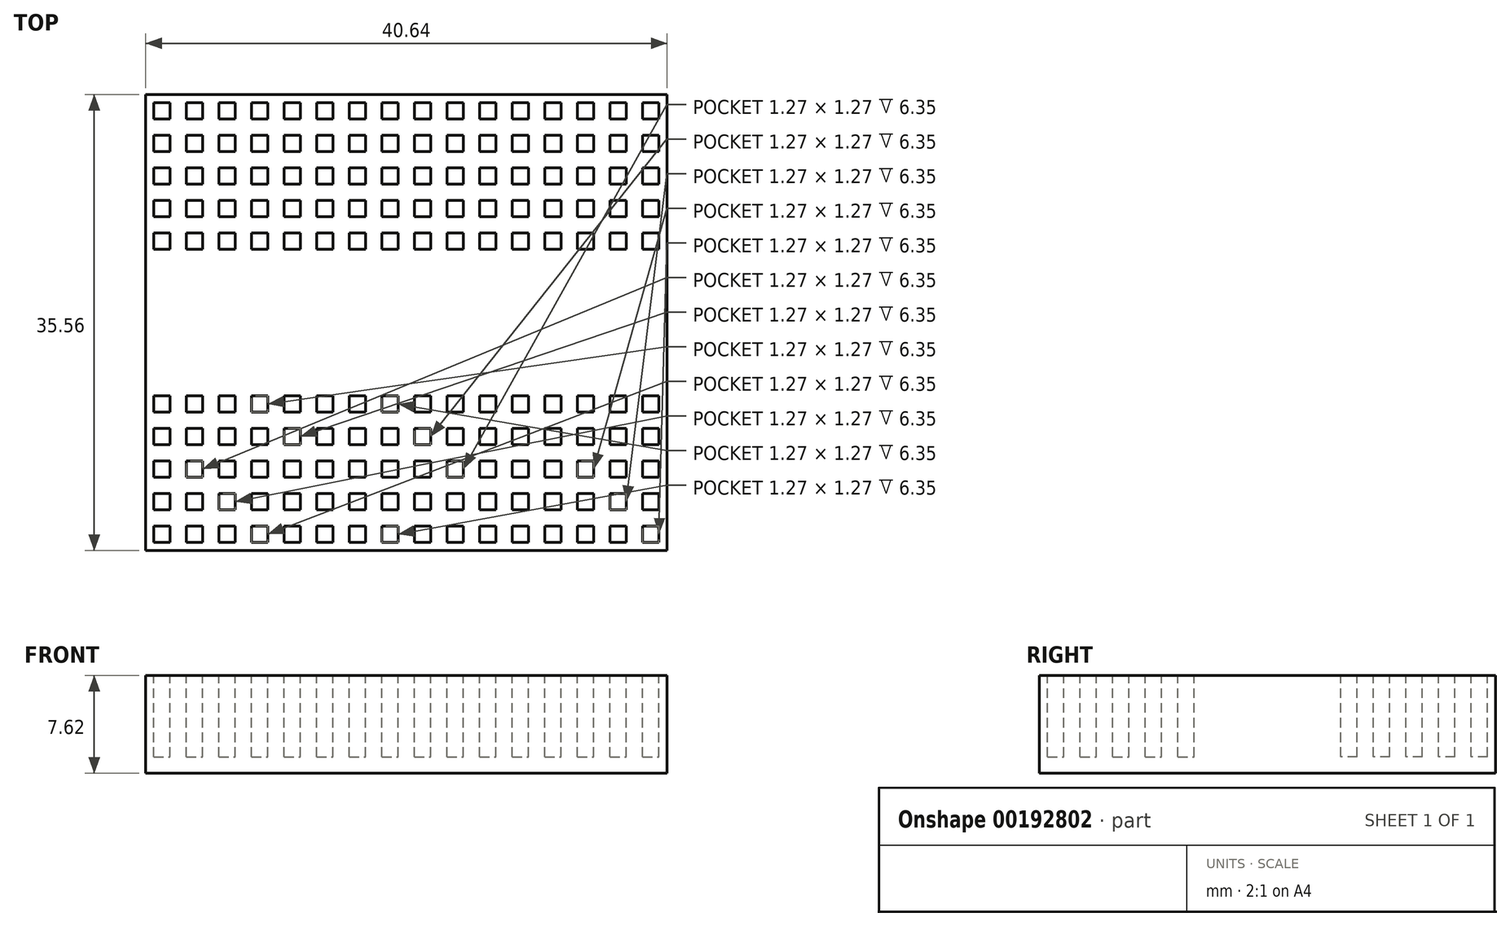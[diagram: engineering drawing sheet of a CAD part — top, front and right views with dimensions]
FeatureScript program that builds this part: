
annotation { "Feature Type Name" : "Feature", "Feature Type Description" : "" }
export const myFeature = defineFeature(function(context is Context, id is Id, definition is map)
    precondition{}
    {
        {
            var Q0;
            Q0=qCreatedBy(makeId("Top.planeOp"),FACE);
            var sketch = newSketch(context, id + "F0", { "sketchPlane" : qUnion([Q0])});
            skLineSegment(sketch, "E0.bottom", {"start": v(-20.32, 17.78) * mm, "end": v(20.32, 17.78) * mm});
            skLineSegment(sketch, "E0.top", {"start": v(-20.32, -17.78) * mm, "end": v(20.32, -17.78) * mm});
            skLineSegment(sketch, "E0.left", {"start": v(-20.32, 17.78) * mm, "end": v(-20.32, -17.78) * mm});
            skLineSegment(sketch, "E0.right", {"start": v(20.32, 17.78) * mm, "end": v(20.32, -17.78) * mm});
            skLineSegment(sketch, "E1", {"start": v(-20.32, 17.78) * mm, "end": v(20.32, -17.78) * mm, "construction": true});
            skSolve(sketch);
        }
        {
            var Q0;
            Q0=qSketchRegion(id+"F0",true);
            extrude(context, id + "F1", {"entities" : qUnion([Q0]), "depth" : 7.62 * mm});
        }
        {
            var Q0;
            Q0=makeQuery(id+"F1.opExtrude","CAP_FACE",FACE,{"disambiguationData":[OSD([sQuery(id+"F0.wireOp",EDGE,"E0.bottom"),sQuery(id+"F0.wireOp",EDGE,"E0.top"),sQuery(id+"F0.wireOp",EDGE,"E0.left"),sQuery(id+"F0.wireOp",EDGE,"E0.right")])],"isStart":false});
            var sketch = newSketch(context, id + "F2", { "sketchPlane" : qUnion([Q0])});
            skLineSegment(sketch, "E2.bottom", {"start": v(-19.69, 17.15) * mm, "end": v(-18.42, 17.15) * mm});
            skLineSegment(sketch, "E2.top", {"start": v(-19.69, 15.88) * mm, "end": v(-18.42, 15.88) * mm});
            skLineSegment(sketch, "E2.left", {"start": v(-19.69, 17.15) * mm, "end": v(-19.69, 15.88) * mm});
            skLineSegment(sketch, "E2.right", {"start": v(-18.42, 17.15) * mm, "end": v(-18.42, 15.88) * mm});
            skLineSegment(sketch, "E3.0.1.0", {"start": v(-19.69, 14.6) * mm, "end": v(-18.42, 14.6) * mm});
            skLineSegment(sketch, "E3.0.1.1", {"start": v(-19.69, 14.6) * mm, "end": v(-19.69, 13.34) * mm});
            skLineSegment(sketch, "E3.0.1.2", {"start": v(-18.42, 14.6) * mm, "end": v(-18.42, 13.34) * mm});
            skLineSegment(sketch, "E3.0.1.3", {"start": v(-19.69, 13.34) * mm, "end": v(-18.42, 13.34) * mm});
            skLineSegment(sketch, "E3.0.2.0", {"start": v(-19.69, 12.07) * mm, "end": v(-18.42, 12.07) * mm});
            skLineSegment(sketch, "E3.0.2.1", {"start": v(-19.69, 12.07) * mm, "end": v(-19.69, 10.8) * mm});
            skLineSegment(sketch, "E3.0.2.2", {"start": v(-18.42, 12.07) * mm, "end": v(-18.42, 10.8) * mm});
            skLineSegment(sketch, "E3.0.2.3", {"start": v(-19.69, 10.8) * mm, "end": v(-18.42, 10.8) * mm});
            skLineSegment(sketch, "E3.0.3.0", {"start": v(-19.69, 9.53) * mm, "end": v(-18.42, 9.53) * mm});
            skLineSegment(sketch, "E3.0.3.1", {"start": v(-19.69, 9.53) * mm, "end": v(-19.69, 8.26) * mm});
            skLineSegment(sketch, "E3.0.3.2", {"start": v(-18.42, 9.53) * mm, "end": v(-18.42, 8.26) * mm});
            skLineSegment(sketch, "E3.0.3.3", {"start": v(-19.69, 8.26) * mm, "end": v(-18.42, 8.26) * mm});
            skLineSegment(sketch, "E3.0.4.0", {"start": v(-19.69, 6.99) * mm, "end": v(-18.42, 6.99) * mm});
            skLineSegment(sketch, "E3.0.4.1", {"start": v(-19.69, 6.99) * mm, "end": v(-19.69, 5.72) * mm});
            skLineSegment(sketch, "E3.0.4.2", {"start": v(-18.42, 6.99) * mm, "end": v(-18.42, 5.72) * mm});
            skLineSegment(sketch, "E3.0.4.3", {"start": v(-19.69, 5.72) * mm, "end": v(-18.42, 5.72) * mm});
            skLineSegment(sketch, "E3.1.0.0", {"start": v(-17.15, 17.15) * mm, "end": v(-15.88, 17.15) * mm});
            skLineSegment(sketch, "E3.1.0.1", {"start": v(-17.15, 17.15) * mm, "end": v(-17.15, 15.88) * mm});
            skLineSegment(sketch, "E3.1.0.2", {"start": v(-15.88, 17.15) * mm, "end": v(-15.88, 15.88) * mm});
            skLineSegment(sketch, "E3.1.0.3", {"start": v(-17.15, 15.88) * mm, "end": v(-15.88, 15.88) * mm});
            skLineSegment(sketch, "E3.1.1.0", {"start": v(-17.15, 14.6) * mm, "end": v(-15.88, 14.6) * mm});
            skLineSegment(sketch, "E3.1.1.1", {"start": v(-17.15, 14.6) * mm, "end": v(-17.15, 13.34) * mm});
            skLineSegment(sketch, "E3.1.1.2", {"start": v(-15.88, 14.6) * mm, "end": v(-15.88, 13.34) * mm});
            skLineSegment(sketch, "E3.1.1.3", {"start": v(-17.15, 13.34) * mm, "end": v(-15.88, 13.34) * mm});
            skLineSegment(sketch, "E3.1.2.0", {"start": v(-17.15, 12.07) * mm, "end": v(-15.88, 12.07) * mm});
            skLineSegment(sketch, "E3.1.2.1", {"start": v(-17.15, 12.07) * mm, "end": v(-17.15, 10.8) * mm});
            skLineSegment(sketch, "E3.1.2.2", {"start": v(-15.88, 12.07) * mm, "end": v(-15.88, 10.8) * mm});
            skLineSegment(sketch, "E3.1.2.3", {"start": v(-17.15, 10.8) * mm, "end": v(-15.88, 10.8) * mm});
            skLineSegment(sketch, "E3.1.3.0", {"start": v(-17.15, 9.53) * mm, "end": v(-15.88, 9.53) * mm});
            skLineSegment(sketch, "E3.1.3.1", {"start": v(-17.15, 9.53) * mm, "end": v(-17.15, 8.26) * mm});
            skLineSegment(sketch, "E3.1.3.2", {"start": v(-15.88, 9.53) * mm, "end": v(-15.88, 8.26) * mm});
            skLineSegment(sketch, "E3.1.3.3", {"start": v(-17.15, 8.26) * mm, "end": v(-15.88, 8.26) * mm});
            skLineSegment(sketch, "E3.1.4.0", {"start": v(-17.15, 6.99) * mm, "end": v(-15.88, 6.99) * mm});
            skLineSegment(sketch, "E3.1.4.1", {"start": v(-17.15, 6.99) * mm, "end": v(-17.15, 5.72) * mm});
            skLineSegment(sketch, "E3.1.4.2", {"start": v(-15.88, 6.99) * mm, "end": v(-15.88, 5.72) * mm});
            skLineSegment(sketch, "E3.1.4.3", {"start": v(-17.15, 5.72) * mm, "end": v(-15.88, 5.72) * mm});
            skLineSegment(sketch, "E3.2.0.0", {"start": v(-14.6, 17.15) * mm, "end": v(-13.34, 17.15) * mm});
            skLineSegment(sketch, "E3.2.0.1", {"start": v(-14.6, 17.15) * mm, "end": v(-14.6, 15.88) * mm});
            skLineSegment(sketch, "E3.2.0.2", {"start": v(-13.34, 17.15) * mm, "end": v(-13.34, 15.88) * mm});
            skLineSegment(sketch, "E3.2.0.3", {"start": v(-14.6, 15.88) * mm, "end": v(-13.34, 15.88) * mm});
            skLineSegment(sketch, "E3.2.1.0", {"start": v(-14.6, 14.6) * mm, "end": v(-13.34, 14.6) * mm});
            skLineSegment(sketch, "E3.2.1.1", {"start": v(-14.6, 14.6) * mm, "end": v(-14.6, 13.34) * mm});
            skLineSegment(sketch, "E3.2.1.2", {"start": v(-13.34, 14.6) * mm, "end": v(-13.34, 13.34) * mm});
            skLineSegment(sketch, "E3.2.1.3", {"start": v(-14.6, 13.34) * mm, "end": v(-13.34, 13.34) * mm});
            skLineSegment(sketch, "E3.2.2.0", {"start": v(-14.6, 12.07) * mm, "end": v(-13.34, 12.07) * mm});
            skLineSegment(sketch, "E3.2.2.1", {"start": v(-14.6, 12.07) * mm, "end": v(-14.6, 10.8) * mm});
            skLineSegment(sketch, "E3.2.2.2", {"start": v(-13.34, 12.07) * mm, "end": v(-13.34, 10.8) * mm});
            skLineSegment(sketch, "E3.2.2.3", {"start": v(-14.6, 10.8) * mm, "end": v(-13.34, 10.8) * mm});
            skLineSegment(sketch, "E3.2.3.0", {"start": v(-14.6, 9.53) * mm, "end": v(-13.34, 9.53) * mm});
            skLineSegment(sketch, "E3.2.3.1", {"start": v(-14.6, 9.53) * mm, "end": v(-14.6, 8.26) * mm});
            skLineSegment(sketch, "E3.2.3.2", {"start": v(-13.34, 9.53) * mm, "end": v(-13.34, 8.26) * mm});
            skLineSegment(sketch, "E3.2.3.3", {"start": v(-14.6, 8.26) * mm, "end": v(-13.34, 8.26) * mm});
            skLineSegment(sketch, "E3.2.4.0", {"start": v(-14.6, 6.99) * mm, "end": v(-13.34, 6.99) * mm});
            skLineSegment(sketch, "E3.2.4.1", {"start": v(-14.6, 6.99) * mm, "end": v(-14.6, 5.72) * mm});
            skLineSegment(sketch, "E3.2.4.2", {"start": v(-13.34, 6.99) * mm, "end": v(-13.34, 5.72) * mm});
            skLineSegment(sketch, "E3.2.4.3", {"start": v(-14.6, 5.72) * mm, "end": v(-13.34, 5.72) * mm});
            skLineSegment(sketch, "E3.3.0.0", {"start": v(-12.07, 17.15) * mm, "end": v(-10.8, 17.15) * mm});
            skLineSegment(sketch, "E3.3.0.1", {"start": v(-12.07, 17.15) * mm, "end": v(-12.07, 15.88) * mm});
            skLineSegment(sketch, "E3.3.0.2", {"start": v(-10.8, 17.15) * mm, "end": v(-10.8, 15.88) * mm});
            skLineSegment(sketch, "E3.3.0.3", {"start": v(-12.07, 15.88) * mm, "end": v(-10.8, 15.88) * mm});
            skLineSegment(sketch, "E3.3.1.0", {"start": v(-12.07, 14.6) * mm, "end": v(-10.8, 14.6) * mm});
            skLineSegment(sketch, "E3.3.1.1", {"start": v(-12.07, 14.6) * mm, "end": v(-12.07, 13.34) * mm});
            skLineSegment(sketch, "E3.3.1.2", {"start": v(-10.8, 14.6) * mm, "end": v(-10.8, 13.34) * mm});
            skLineSegment(sketch, "E3.3.1.3", {"start": v(-12.07, 13.34) * mm, "end": v(-10.8, 13.34) * mm});
            skLineSegment(sketch, "E3.3.2.0", {"start": v(-12.07, 12.07) * mm, "end": v(-10.8, 12.07) * mm});
            skLineSegment(sketch, "E3.3.2.1", {"start": v(-12.07, 12.07) * mm, "end": v(-12.07, 10.8) * mm});
            skLineSegment(sketch, "E3.3.2.2", {"start": v(-10.8, 12.07) * mm, "end": v(-10.8, 10.8) * mm});
            skLineSegment(sketch, "E3.3.2.3", {"start": v(-12.07, 10.8) * mm, "end": v(-10.8, 10.8) * mm});
            skLineSegment(sketch, "E3.3.3.0", {"start": v(-12.07, 9.53) * mm, "end": v(-10.8, 9.53) * mm});
            skLineSegment(sketch, "E3.3.3.1", {"start": v(-12.07, 9.53) * mm, "end": v(-12.07, 8.26) * mm});
            skLineSegment(sketch, "E3.3.3.2", {"start": v(-10.8, 9.53) * mm, "end": v(-10.8, 8.26) * mm});
            skLineSegment(sketch, "E3.3.3.3", {"start": v(-12.07, 8.26) * mm, "end": v(-10.8, 8.26) * mm});
            skLineSegment(sketch, "E3.3.4.0", {"start": v(-12.07, 6.99) * mm, "end": v(-10.8, 6.99) * mm});
            skLineSegment(sketch, "E3.3.4.1", {"start": v(-12.07, 6.99) * mm, "end": v(-12.07, 5.72) * mm});
            skLineSegment(sketch, "E3.3.4.2", {"start": v(-10.8, 6.99) * mm, "end": v(-10.8, 5.72) * mm});
            skLineSegment(sketch, "E3.3.4.3", {"start": v(-12.07, 5.72) * mm, "end": v(-10.8, 5.72) * mm});
            skLineSegment(sketch, "E3.4.0.0", {"start": v(-9.53, 17.15) * mm, "end": v(-8.26, 17.15) * mm});
            skLineSegment(sketch, "E3.4.0.1", {"start": v(-9.53, 17.15) * mm, "end": v(-9.53, 15.88) * mm});
            skLineSegment(sketch, "E3.4.0.2", {"start": v(-8.26, 17.15) * mm, "end": v(-8.26, 15.88) * mm});
            skLineSegment(sketch, "E3.4.0.3", {"start": v(-9.53, 15.88) * mm, "end": v(-8.26, 15.88) * mm});
            skLineSegment(sketch, "E3.4.1.0", {"start": v(-9.53, 14.6) * mm, "end": v(-8.26, 14.6) * mm});
            skLineSegment(sketch, "E3.4.1.1", {"start": v(-9.53, 14.6) * mm, "end": v(-9.53, 13.34) * mm});
            skLineSegment(sketch, "E3.4.1.2", {"start": v(-8.26, 14.6) * mm, "end": v(-8.26, 13.34) * mm});
            skLineSegment(sketch, "E3.4.1.3", {"start": v(-9.53, 13.34) * mm, "end": v(-8.26, 13.34) * mm});
            skLineSegment(sketch, "E3.4.2.0", {"start": v(-9.53, 12.07) * mm, "end": v(-8.26, 12.07) * mm});
            skLineSegment(sketch, "E3.4.2.1", {"start": v(-9.53, 12.07) * mm, "end": v(-9.53, 10.8) * mm});
            skLineSegment(sketch, "E3.4.2.2", {"start": v(-8.26, 12.07) * mm, "end": v(-8.26, 10.8) * mm});
            skLineSegment(sketch, "E3.4.2.3", {"start": v(-9.53, 10.8) * mm, "end": v(-8.26, 10.8) * mm});
            skLineSegment(sketch, "E3.4.3.0", {"start": v(-9.53, 9.53) * mm, "end": v(-8.26, 9.53) * mm});
            skLineSegment(sketch, "E3.4.3.1", {"start": v(-9.53, 9.53) * mm, "end": v(-9.53, 8.26) * mm});
            skLineSegment(sketch, "E3.4.3.2", {"start": v(-8.26, 9.53) * mm, "end": v(-8.26, 8.26) * mm});
            skLineSegment(sketch, "E3.4.3.3", {"start": v(-9.53, 8.26) * mm, "end": v(-8.26, 8.26) * mm});
            skLineSegment(sketch, "E3.4.4.0", {"start": v(-9.53, 6.99) * mm, "end": v(-8.26, 6.99) * mm});
            skLineSegment(sketch, "E3.4.4.1", {"start": v(-9.53, 6.99) * mm, "end": v(-9.53, 5.72) * mm});
            skLineSegment(sketch, "E3.4.4.2", {"start": v(-8.26, 6.99) * mm, "end": v(-8.26, 5.72) * mm});
            skLineSegment(sketch, "E3.4.4.3", {"start": v(-9.53, 5.72) * mm, "end": v(-8.26, 5.72) * mm});
            skLineSegment(sketch, "E3.5.0.0", {"start": v(-6.99, 17.15) * mm, "end": v(-5.72, 17.15) * mm});
            skLineSegment(sketch, "E3.5.0.1", {"start": v(-6.99, 17.15) * mm, "end": v(-6.99, 15.88) * mm});
            skLineSegment(sketch, "E3.5.0.2", {"start": v(-5.72, 17.15) * mm, "end": v(-5.72, 15.88) * mm});
            skLineSegment(sketch, "E3.5.0.3", {"start": v(-6.99, 15.88) * mm, "end": v(-5.72, 15.88) * mm});
            skLineSegment(sketch, "E3.5.1.0", {"start": v(-6.99, 14.6) * mm, "end": v(-5.72, 14.6) * mm});
            skLineSegment(sketch, "E3.5.1.1", {"start": v(-6.99, 14.6) * mm, "end": v(-6.99, 13.34) * mm});
            skLineSegment(sketch, "E3.5.1.2", {"start": v(-5.72, 14.6) * mm, "end": v(-5.72, 13.34) * mm});
            skLineSegment(sketch, "E3.5.1.3", {"start": v(-6.99, 13.34) * mm, "end": v(-5.72, 13.34) * mm});
            skLineSegment(sketch, "E3.5.2.0", {"start": v(-6.99, 12.07) * mm, "end": v(-5.72, 12.07) * mm});
            skLineSegment(sketch, "E3.5.2.1", {"start": v(-6.99, 12.07) * mm, "end": v(-6.99, 10.8) * mm});
            skLineSegment(sketch, "E3.5.2.2", {"start": v(-5.72, 12.07) * mm, "end": v(-5.72, 10.8) * mm});
            skLineSegment(sketch, "E3.5.2.3", {"start": v(-6.99, 10.8) * mm, "end": v(-5.72, 10.8) * mm});
            skLineSegment(sketch, "E3.5.3.0", {"start": v(-6.99, 9.53) * mm, "end": v(-5.72, 9.53) * mm});
            skLineSegment(sketch, "E3.5.3.1", {"start": v(-6.99, 9.53) * mm, "end": v(-6.99, 8.26) * mm});
            skLineSegment(sketch, "E3.5.3.2", {"start": v(-5.72, 9.53) * mm, "end": v(-5.72, 8.26) * mm});
            skLineSegment(sketch, "E3.5.3.3", {"start": v(-6.99, 8.26) * mm, "end": v(-5.72, 8.26) * mm});
            skLineSegment(sketch, "E3.5.4.0", {"start": v(-6.99, 6.99) * mm, "end": v(-5.72, 6.99) * mm});
            skLineSegment(sketch, "E3.5.4.1", {"start": v(-6.99, 6.99) * mm, "end": v(-6.99, 5.72) * mm});
            skLineSegment(sketch, "E3.5.4.2", {"start": v(-5.72, 6.99) * mm, "end": v(-5.72, 5.72) * mm});
            skLineSegment(sketch, "E3.5.4.3", {"start": v(-6.99, 5.72) * mm, "end": v(-5.72, 5.72) * mm});
            skLineSegment(sketch, "E3.6.0.0", {"start": v(-4.45, 17.15) * mm, "end": v(-3.18, 17.15) * mm});
            skLineSegment(sketch, "E3.6.0.1", {"start": v(-4.45, 17.15) * mm, "end": v(-4.45, 15.88) * mm});
            skLineSegment(sketch, "E3.6.0.2", {"start": v(-3.18, 17.15) * mm, "end": v(-3.18, 15.88) * mm});
            skLineSegment(sketch, "E3.6.0.3", {"start": v(-4.45, 15.88) * mm, "end": v(-3.18, 15.88) * mm});
            skLineSegment(sketch, "E3.6.1.0", {"start": v(-4.45, 14.6) * mm, "end": v(-3.18, 14.6) * mm});
            skLineSegment(sketch, "E3.6.1.1", {"start": v(-4.45, 14.6) * mm, "end": v(-4.45, 13.34) * mm});
            skLineSegment(sketch, "E3.6.1.2", {"start": v(-3.18, 14.6) * mm, "end": v(-3.18, 13.34) * mm});
            skLineSegment(sketch, "E3.6.1.3", {"start": v(-4.45, 13.34) * mm, "end": v(-3.18, 13.34) * mm});
            skLineSegment(sketch, "E3.6.2.0", {"start": v(-4.45, 12.07) * mm, "end": v(-3.18, 12.07) * mm});
            skLineSegment(sketch, "E3.6.2.1", {"start": v(-4.45, 12.07) * mm, "end": v(-4.45, 10.8) * mm});
            skLineSegment(sketch, "E3.6.2.2", {"start": v(-3.18, 12.07) * mm, "end": v(-3.18, 10.8) * mm});
            skLineSegment(sketch, "E3.6.2.3", {"start": v(-4.45, 10.8) * mm, "end": v(-3.18, 10.8) * mm});
            skLineSegment(sketch, "E3.6.3.0", {"start": v(-4.45, 9.53) * mm, "end": v(-3.18, 9.53) * mm});
            skLineSegment(sketch, "E3.6.3.1", {"start": v(-4.45, 9.53) * mm, "end": v(-4.45, 8.26) * mm});
            skLineSegment(sketch, "E3.6.3.2", {"start": v(-3.18, 9.53) * mm, "end": v(-3.18, 8.26) * mm});
            skLineSegment(sketch, "E3.6.3.3", {"start": v(-4.45, 8.26) * mm, "end": v(-3.18, 8.26) * mm});
            skLineSegment(sketch, "E3.6.4.0", {"start": v(-4.45, 6.99) * mm, "end": v(-3.18, 6.99) * mm});
            skLineSegment(sketch, "E3.6.4.1", {"start": v(-4.45, 6.99) * mm, "end": v(-4.45, 5.72) * mm});
            skLineSegment(sketch, "E3.6.4.2", {"start": v(-3.18, 6.99) * mm, "end": v(-3.18, 5.72) * mm});
            skLineSegment(sketch, "E3.6.4.3", {"start": v(-4.45, 5.72) * mm, "end": v(-3.18, 5.72) * mm});
            skLineSegment(sketch, "E3.7.0.0", {"start": v(-1.9, 17.15) * mm, "end": v(-0.64, 17.15) * mm});
            skLineSegment(sketch, "E3.7.0.1", {"start": v(-1.9, 17.15) * mm, "end": v(-1.9, 15.88) * mm});
            skLineSegment(sketch, "E3.7.0.2", {"start": v(-0.63, 17.15) * mm, "end": v(-0.64, 15.88) * mm});
            skLineSegment(sketch, "E3.7.0.3", {"start": v(-1.9, 15.88) * mm, "end": v(-0.64, 15.88) * mm});
            skLineSegment(sketch, "E3.7.1.0", {"start": v(-1.9, 14.6) * mm, "end": v(-0.64, 14.6) * mm});
            skLineSegment(sketch, "E3.7.1.1", {"start": v(-1.9, 14.6) * mm, "end": v(-1.9, 13.34) * mm});
            skLineSegment(sketch, "E3.7.1.2", {"start": v(-0.63, 14.6) * mm, "end": v(-0.64, 13.34) * mm});
            skLineSegment(sketch, "E3.7.1.3", {"start": v(-1.9, 13.34) * mm, "end": v(-0.64, 13.34) * mm});
            skLineSegment(sketch, "E3.7.2.0", {"start": v(-1.9, 12.07) * mm, "end": v(-0.64, 12.07) * mm});
            skLineSegment(sketch, "E3.7.2.1", {"start": v(-1.9, 12.07) * mm, "end": v(-1.9, 10.8) * mm});
            skLineSegment(sketch, "E3.7.2.2", {"start": v(-0.63, 12.07) * mm, "end": v(-0.64, 10.8) * mm});
            skLineSegment(sketch, "E3.7.2.3", {"start": v(-1.9, 10.8) * mm, "end": v(-0.64, 10.8) * mm});
            skLineSegment(sketch, "E3.7.3.0", {"start": v(-1.9, 9.53) * mm, "end": v(-0.64, 9.53) * mm});
            skLineSegment(sketch, "E3.7.3.1", {"start": v(-1.9, 9.53) * mm, "end": v(-1.9, 8.26) * mm});
            skLineSegment(sketch, "E3.7.3.2", {"start": v(-0.63, 9.53) * mm, "end": v(-0.64, 8.26) * mm});
            skLineSegment(sketch, "E3.7.3.3", {"start": v(-1.9, 8.26) * mm, "end": v(-0.64, 8.26) * mm});
            skLineSegment(sketch, "E3.7.4.0", {"start": v(-1.9, 6.99) * mm, "end": v(-0.64, 6.99) * mm});
            skLineSegment(sketch, "E3.7.4.1", {"start": v(-1.9, 6.99) * mm, "end": v(-1.9, 5.72) * mm});
            skLineSegment(sketch, "E3.7.4.2", {"start": v(-0.63, 6.99) * mm, "end": v(-0.64, 5.72) * mm});
            skLineSegment(sketch, "E3.7.4.3", {"start": v(-1.9, 5.72) * mm, "end": v(-0.64, 5.72) * mm});
            skLineSegment(sketch, "E3.8.0.0", {"start": v(0.64, 17.15) * mm, "end": v(1.9, 17.15) * mm});
            skLineSegment(sketch, "E3.8.0.1", {"start": v(0.64, 17.15) * mm, "end": v(0.64, 15.88) * mm});
            skLineSegment(sketch, "E3.8.0.2", {"start": v(1.9, 17.15) * mm, "end": v(1.9, 15.88) * mm});
            skLineSegment(sketch, "E3.8.0.3", {"start": v(0.64, 15.88) * mm, "end": v(1.9, 15.88) * mm});
            skLineSegment(sketch, "E3.8.1.0", {"start": v(0.64, 14.6) * mm, "end": v(1.9, 14.6) * mm});
            skLineSegment(sketch, "E3.8.1.1", {"start": v(0.64, 14.6) * mm, "end": v(0.64, 13.34) * mm});
            skLineSegment(sketch, "E3.8.1.2", {"start": v(1.9, 14.6) * mm, "end": v(1.9, 13.34) * mm});
            skLineSegment(sketch, "E3.8.1.3", {"start": v(0.64, 13.34) * mm, "end": v(1.9, 13.34) * mm});
            skLineSegment(sketch, "E3.8.2.0", {"start": v(0.64, 12.07) * mm, "end": v(1.9, 12.07) * mm});
            skLineSegment(sketch, "E3.8.2.1", {"start": v(0.64, 12.07) * mm, "end": v(0.64, 10.8) * mm});
            skLineSegment(sketch, "E3.8.2.2", {"start": v(1.9, 12.07) * mm, "end": v(1.9, 10.8) * mm});
            skLineSegment(sketch, "E3.8.2.3", {"start": v(0.64, 10.8) * mm, "end": v(1.9, 10.8) * mm});
            skLineSegment(sketch, "E3.8.3.0", {"start": v(0.64, 9.53) * mm, "end": v(1.9, 9.53) * mm});
            skLineSegment(sketch, "E3.8.3.1", {"start": v(0.64, 9.53) * mm, "end": v(0.64, 8.26) * mm});
            skLineSegment(sketch, "E3.8.3.2", {"start": v(1.9, 9.53) * mm, "end": v(1.9, 8.26) * mm});
            skLineSegment(sketch, "E3.8.3.3", {"start": v(0.64, 8.26) * mm, "end": v(1.9, 8.26) * mm});
            skLineSegment(sketch, "E3.8.4.0", {"start": v(0.64, 6.99) * mm, "end": v(1.9, 6.99) * mm});
            skLineSegment(sketch, "E3.8.4.1", {"start": v(0.64, 6.99) * mm, "end": v(0.64, 5.72) * mm});
            skLineSegment(sketch, "E3.8.4.2", {"start": v(1.9, 6.99) * mm, "end": v(1.9, 5.72) * mm});
            skLineSegment(sketch, "E3.8.4.3", {"start": v(0.64, 5.72) * mm, "end": v(1.9, 5.72) * mm});
            skLineSegment(sketch, "E3.9.0.0", {"start": v(3.18, 17.15) * mm, "end": v(4.45, 17.15) * mm});
            skLineSegment(sketch, "E3.9.0.1", {"start": v(3.18, 17.15) * mm, "end": v(3.18, 15.88) * mm});
            skLineSegment(sketch, "E3.9.0.2", {"start": v(4.45, 17.15) * mm, "end": v(4.45, 15.88) * mm});
            skLineSegment(sketch, "E3.9.0.3", {"start": v(3.18, 15.88) * mm, "end": v(4.45, 15.88) * mm});
            skLineSegment(sketch, "E3.9.1.0", {"start": v(3.18, 14.6) * mm, "end": v(4.45, 14.6) * mm});
            skLineSegment(sketch, "E3.9.1.1", {"start": v(3.18, 14.6) * mm, "end": v(3.18, 13.34) * mm});
            skLineSegment(sketch, "E3.9.1.2", {"start": v(4.45, 14.6) * mm, "end": v(4.45, 13.34) * mm});
            skLineSegment(sketch, "E3.9.1.3", {"start": v(3.18, 13.34) * mm, "end": v(4.45, 13.34) * mm});
            skLineSegment(sketch, "E3.9.2.0", {"start": v(3.18, 12.07) * mm, "end": v(4.45, 12.07) * mm});
            skLineSegment(sketch, "E3.9.2.1", {"start": v(3.18, 12.07) * mm, "end": v(3.18, 10.8) * mm});
            skLineSegment(sketch, "E3.9.2.2", {"start": v(4.45, 12.07) * mm, "end": v(4.45, 10.8) * mm});
            skLineSegment(sketch, "E3.9.2.3", {"start": v(3.18, 10.8) * mm, "end": v(4.45, 10.8) * mm});
            skLineSegment(sketch, "E3.9.3.0", {"start": v(3.18, 9.53) * mm, "end": v(4.45, 9.53) * mm});
            skLineSegment(sketch, "E3.9.3.1", {"start": v(3.18, 9.53) * mm, "end": v(3.18, 8.26) * mm});
            skLineSegment(sketch, "E3.9.3.2", {"start": v(4.45, 9.53) * mm, "end": v(4.45, 8.26) * mm});
            skLineSegment(sketch, "E3.9.3.3", {"start": v(3.18, 8.26) * mm, "end": v(4.45, 8.26) * mm});
            skLineSegment(sketch, "E3.9.4.0", {"start": v(3.18, 6.99) * mm, "end": v(4.45, 6.99) * mm});
            skLineSegment(sketch, "E3.9.4.1", {"start": v(3.18, 6.99) * mm, "end": v(3.18, 5.72) * mm});
            skLineSegment(sketch, "E3.9.4.2", {"start": v(4.45, 6.99) * mm, "end": v(4.45, 5.72) * mm});
            skLineSegment(sketch, "E3.9.4.3", {"start": v(3.18, 5.72) * mm, "end": v(4.45, 5.72) * mm});
            skLineSegment(sketch, "E3.10.0.0", {"start": v(5.72, 17.15) * mm, "end": v(6.99, 17.15) * mm});
            skLineSegment(sketch, "E3.10.0.1", {"start": v(5.72, 17.15) * mm, "end": v(5.72, 15.88) * mm});
            skLineSegment(sketch, "E3.10.0.2", {"start": v(6.99, 17.15) * mm, "end": v(6.99, 15.88) * mm});
            skLineSegment(sketch, "E3.10.0.3", {"start": v(5.72, 15.88) * mm, "end": v(6.99, 15.88) * mm});
            skLineSegment(sketch, "E3.10.1.0", {"start": v(5.72, 14.6) * mm, "end": v(6.99, 14.6) * mm});
            skLineSegment(sketch, "E3.10.1.1", {"start": v(5.72, 14.6) * mm, "end": v(5.72, 13.34) * mm});
            skLineSegment(sketch, "E3.10.1.2", {"start": v(6.99, 14.6) * mm, "end": v(6.99, 13.34) * mm});
            skLineSegment(sketch, "E3.10.1.3", {"start": v(5.72, 13.34) * mm, "end": v(6.99, 13.34) * mm});
            skLineSegment(sketch, "E3.10.2.0", {"start": v(5.72, 12.07) * mm, "end": v(6.99, 12.07) * mm});
            skLineSegment(sketch, "E3.10.2.1", {"start": v(5.72, 12.07) * mm, "end": v(5.72, 10.8) * mm});
            skLineSegment(sketch, "E3.10.2.2", {"start": v(6.99, 12.07) * mm, "end": v(6.99, 10.8) * mm});
            skLineSegment(sketch, "E3.10.2.3", {"start": v(5.72, 10.8) * mm, "end": v(6.99, 10.8) * mm});
            skLineSegment(sketch, "E3.10.3.0", {"start": v(5.72, 9.53) * mm, "end": v(6.99, 9.53) * mm});
            skLineSegment(sketch, "E3.10.3.1", {"start": v(5.72, 9.53) * mm, "end": v(5.72, 8.26) * mm});
            skLineSegment(sketch, "E3.10.3.2", {"start": v(6.99, 9.53) * mm, "end": v(6.99, 8.26) * mm});
            skLineSegment(sketch, "E3.10.3.3", {"start": v(5.72, 8.26) * mm, "end": v(6.99, 8.26) * mm});
            skLineSegment(sketch, "E3.10.4.0", {"start": v(5.72, 6.99) * mm, "end": v(6.99, 6.99) * mm});
            skLineSegment(sketch, "E3.10.4.1", {"start": v(5.72, 6.99) * mm, "end": v(5.72, 5.72) * mm});
            skLineSegment(sketch, "E3.10.4.2", {"start": v(6.99, 6.99) * mm, "end": v(6.99, 5.72) * mm});
            skLineSegment(sketch, "E3.10.4.3", {"start": v(5.72, 5.72) * mm, "end": v(6.99, 5.72) * mm});
            skLineSegment(sketch, "E3.11.0.0", {"start": v(8.26, 17.15) * mm, "end": v(9.53, 17.15) * mm});
            skLineSegment(sketch, "E3.11.0.1", {"start": v(8.26, 17.15) * mm, "end": v(8.26, 15.88) * mm});
            skLineSegment(sketch, "E3.11.0.2", {"start": v(9.53, 17.15) * mm, "end": v(9.53, 15.88) * mm});
            skLineSegment(sketch, "E3.11.0.3", {"start": v(8.26, 15.88) * mm, "end": v(9.53, 15.88) * mm});
            skLineSegment(sketch, "E3.11.1.0", {"start": v(8.26, 14.6) * mm, "end": v(9.53, 14.6) * mm});
            skLineSegment(sketch, "E3.11.1.1", {"start": v(8.26, 14.6) * mm, "end": v(8.26, 13.34) * mm});
            skLineSegment(sketch, "E3.11.1.2", {"start": v(9.53, 14.6) * mm, "end": v(9.53, 13.34) * mm});
            skLineSegment(sketch, "E3.11.1.3", {"start": v(8.26, 13.34) * mm, "end": v(9.53, 13.34) * mm});
            skLineSegment(sketch, "E3.11.2.0", {"start": v(8.26, 12.07) * mm, "end": v(9.53, 12.07) * mm});
            skLineSegment(sketch, "E3.11.2.1", {"start": v(8.26, 12.07) * mm, "end": v(8.26, 10.8) * mm});
            skLineSegment(sketch, "E3.11.2.2", {"start": v(9.53, 12.07) * mm, "end": v(9.53, 10.8) * mm});
            skLineSegment(sketch, "E3.11.2.3", {"start": v(8.26, 10.8) * mm, "end": v(9.53, 10.8) * mm});
            skLineSegment(sketch, "E3.11.3.0", {"start": v(8.26, 9.53) * mm, "end": v(9.53, 9.53) * mm});
            skLineSegment(sketch, "E3.11.3.1", {"start": v(8.26, 9.53) * mm, "end": v(8.26, 8.26) * mm});
            skLineSegment(sketch, "E3.11.3.2", {"start": v(9.53, 9.53) * mm, "end": v(9.53, 8.26) * mm});
            skLineSegment(sketch, "E3.11.3.3", {"start": v(8.26, 8.26) * mm, "end": v(9.53, 8.26) * mm});
            skLineSegment(sketch, "E3.11.4.0", {"start": v(8.26, 6.99) * mm, "end": v(9.53, 6.99) * mm});
            skLineSegment(sketch, "E3.11.4.1", {"start": v(8.26, 6.99) * mm, "end": v(8.26, 5.72) * mm});
            skLineSegment(sketch, "E3.11.4.2", {"start": v(9.53, 6.99) * mm, "end": v(9.53, 5.72) * mm});
            skLineSegment(sketch, "E3.11.4.3", {"start": v(8.26, 5.72) * mm, "end": v(9.53, 5.72) * mm});
            skLineSegment(sketch, "E3.12.0.0", {"start": v(10.8, 17.15) * mm, "end": v(12.07, 17.15) * mm});
            skLineSegment(sketch, "E3.12.0.1", {"start": v(10.8, 17.15) * mm, "end": v(10.8, 15.88) * mm});
            skLineSegment(sketch, "E3.12.0.2", {"start": v(12.07, 17.15) * mm, "end": v(12.07, 15.88) * mm});
            skLineSegment(sketch, "E3.12.0.3", {"start": v(10.8, 15.88) * mm, "end": v(12.07, 15.88) * mm});
            skLineSegment(sketch, "E3.12.1.0", {"start": v(10.8, 14.6) * mm, "end": v(12.07, 14.6) * mm});
            skLineSegment(sketch, "E3.12.1.1", {"start": v(10.8, 14.6) * mm, "end": v(10.8, 13.34) * mm});
            skLineSegment(sketch, "E3.12.1.2", {"start": v(12.07, 14.6) * mm, "end": v(12.07, 13.34) * mm});
            skLineSegment(sketch, "E3.12.1.3", {"start": v(10.8, 13.34) * mm, "end": v(12.07, 13.34) * mm});
            skLineSegment(sketch, "E3.12.2.0", {"start": v(10.8, 12.07) * mm, "end": v(12.07, 12.07) * mm});
            skLineSegment(sketch, "E3.12.2.1", {"start": v(10.8, 12.07) * mm, "end": v(10.8, 10.8) * mm});
            skLineSegment(sketch, "E3.12.2.2", {"start": v(12.07, 12.07) * mm, "end": v(12.07, 10.8) * mm});
            skLineSegment(sketch, "E3.12.2.3", {"start": v(10.8, 10.8) * mm, "end": v(12.07, 10.8) * mm});
            skLineSegment(sketch, "E3.12.3.0", {"start": v(10.8, 9.53) * mm, "end": v(12.07, 9.53) * mm});
            skLineSegment(sketch, "E3.12.3.1", {"start": v(10.8, 9.53) * mm, "end": v(10.8, 8.26) * mm});
            skLineSegment(sketch, "E3.12.3.2", {"start": v(12.07, 9.53) * mm, "end": v(12.07, 8.26) * mm});
            skLineSegment(sketch, "E3.12.3.3", {"start": v(10.8, 8.26) * mm, "end": v(12.07, 8.26) * mm});
            skLineSegment(sketch, "E3.12.4.0", {"start": v(10.8, 6.99) * mm, "end": v(12.07, 6.99) * mm});
            skLineSegment(sketch, "E3.12.4.1", {"start": v(10.8, 6.99) * mm, "end": v(10.8, 5.72) * mm});
            skLineSegment(sketch, "E3.12.4.2", {"start": v(12.07, 6.99) * mm, "end": v(12.07, 5.72) * mm});
            skLineSegment(sketch, "E3.12.4.3", {"start": v(10.8, 5.72) * mm, "end": v(12.07, 5.72) * mm});
            skLineSegment(sketch, "E3.13.0.0", {"start": v(13.34, 17.15) * mm, "end": v(14.6, 17.15) * mm});
            skLineSegment(sketch, "E3.13.0.1", {"start": v(13.34, 17.15) * mm, "end": v(13.34, 15.88) * mm});
            skLineSegment(sketch, "E3.13.0.2", {"start": v(14.6, 17.15) * mm, "end": v(14.6, 15.88) * mm});
            skLineSegment(sketch, "E3.13.0.3", {"start": v(13.34, 15.88) * mm, "end": v(14.6, 15.88) * mm});
            skLineSegment(sketch, "E3.13.1.0", {"start": v(13.34, 14.6) * mm, "end": v(14.6, 14.6) * mm});
            skLineSegment(sketch, "E3.13.1.1", {"start": v(13.34, 14.6) * mm, "end": v(13.34, 13.34) * mm});
            skLineSegment(sketch, "E3.13.1.2", {"start": v(14.6, 14.6) * mm, "end": v(14.6, 13.34) * mm});
            skLineSegment(sketch, "E3.13.1.3", {"start": v(13.34, 13.34) * mm, "end": v(14.6, 13.34) * mm});
            skLineSegment(sketch, "E3.13.2.0", {"start": v(13.34, 12.07) * mm, "end": v(14.6, 12.07) * mm});
            skLineSegment(sketch, "E3.13.2.1", {"start": v(13.34, 12.07) * mm, "end": v(13.34, 10.8) * mm});
            skLineSegment(sketch, "E3.13.2.2", {"start": v(14.6, 12.07) * mm, "end": v(14.6, 10.8) * mm});
            skLineSegment(sketch, "E3.13.2.3", {"start": v(13.34, 10.8) * mm, "end": v(14.6, 10.8) * mm});
            skLineSegment(sketch, "E3.13.3.0", {"start": v(13.34, 9.53) * mm, "end": v(14.6, 9.53) * mm});
            skLineSegment(sketch, "E3.13.3.1", {"start": v(13.34, 9.53) * mm, "end": v(13.34, 8.26) * mm});
            skLineSegment(sketch, "E3.13.3.2", {"start": v(14.6, 9.53) * mm, "end": v(14.6, 8.26) * mm});
            skLineSegment(sketch, "E3.13.3.3", {"start": v(13.34, 8.26) * mm, "end": v(14.6, 8.26) * mm});
            skLineSegment(sketch, "E3.13.4.0", {"start": v(13.34, 6.99) * mm, "end": v(14.6, 6.99) * mm});
            skLineSegment(sketch, "E3.13.4.1", {"start": v(13.34, 6.99) * mm, "end": v(13.34, 5.72) * mm});
            skLineSegment(sketch, "E3.13.4.2", {"start": v(14.6, 6.99) * mm, "end": v(14.6, 5.72) * mm});
            skLineSegment(sketch, "E3.13.4.3", {"start": v(13.34, 5.72) * mm, "end": v(14.6, 5.72) * mm});
            skLineSegment(sketch, "E3.14.0.0", {"start": v(15.88, 17.15) * mm, "end": v(17.15, 17.15) * mm});
            skLineSegment(sketch, "E3.14.0.1", {"start": v(15.88, 17.15) * mm, "end": v(15.88, 15.88) * mm});
            skLineSegment(sketch, "E3.14.0.2", {"start": v(17.15, 17.15) * mm, "end": v(17.15, 15.88) * mm});
            skLineSegment(sketch, "E3.14.0.3", {"start": v(15.88, 15.88) * mm, "end": v(17.15, 15.88) * mm});
            skLineSegment(sketch, "E3.14.1.0", {"start": v(15.88, 14.6) * mm, "end": v(17.15, 14.6) * mm});
            skLineSegment(sketch, "E3.14.1.1", {"start": v(15.88, 14.6) * mm, "end": v(15.88, 13.34) * mm});
            skLineSegment(sketch, "E3.14.1.2", {"start": v(17.15, 14.6) * mm, "end": v(17.15, 13.34) * mm});
            skLineSegment(sketch, "E3.14.1.3", {"start": v(15.88, 13.34) * mm, "end": v(17.15, 13.34) * mm});
            skLineSegment(sketch, "E3.14.2.0", {"start": v(15.88, 12.07) * mm, "end": v(17.15, 12.07) * mm});
            skLineSegment(sketch, "E3.14.2.1", {"start": v(15.88, 12.07) * mm, "end": v(15.88, 10.8) * mm});
            skLineSegment(sketch, "E3.14.2.2", {"start": v(17.15, 12.07) * mm, "end": v(17.15, 10.8) * mm});
            skLineSegment(sketch, "E3.14.2.3", {"start": v(15.88, 10.8) * mm, "end": v(17.15, 10.8) * mm});
            skLineSegment(sketch, "E3.14.3.0", {"start": v(15.88, 9.53) * mm, "end": v(17.15, 9.53) * mm});
            skLineSegment(sketch, "E3.14.3.1", {"start": v(15.88, 9.53) * mm, "end": v(15.88, 8.26) * mm});
            skLineSegment(sketch, "E3.14.3.2", {"start": v(17.15, 9.53) * mm, "end": v(17.15, 8.26) * mm});
            skLineSegment(sketch, "E3.14.3.3", {"start": v(15.88, 8.26) * mm, "end": v(17.15, 8.26) * mm});
            skLineSegment(sketch, "E3.14.4.0", {"start": v(15.88, 6.99) * mm, "end": v(17.15, 6.99) * mm});
            skLineSegment(sketch, "E3.14.4.1", {"start": v(15.88, 6.99) * mm, "end": v(15.88, 5.72) * mm});
            skLineSegment(sketch, "E3.14.4.2", {"start": v(17.15, 6.99) * mm, "end": v(17.15, 5.72) * mm});
            skLineSegment(sketch, "E3.14.4.3", {"start": v(15.88, 5.72) * mm, "end": v(17.15, 5.72) * mm});
            skLineSegment(sketch, "E3.15.0.0", {"start": v(18.42, 17.15) * mm, "end": v(19.69, 17.15) * mm});
            skLineSegment(sketch, "E3.15.0.1", {"start": v(18.42, 17.15) * mm, "end": v(18.42, 15.88) * mm});
            skLineSegment(sketch, "E3.15.0.2", {"start": v(19.69, 17.15) * mm, "end": v(19.69, 15.88) * mm});
            skLineSegment(sketch, "E3.15.0.3", {"start": v(18.42, 15.88) * mm, "end": v(19.69, 15.88) * mm});
            skLineSegment(sketch, "E3.15.1.0", {"start": v(18.42, 14.6) * mm, "end": v(19.69, 14.6) * mm});
            skLineSegment(sketch, "E3.15.1.1", {"start": v(18.42, 14.6) * mm, "end": v(18.42, 13.34) * mm});
            skLineSegment(sketch, "E3.15.1.2", {"start": v(19.69, 14.6) * mm, "end": v(19.69, 13.34) * mm});
            skLineSegment(sketch, "E3.15.1.3", {"start": v(18.42, 13.34) * mm, "end": v(19.69, 13.34) * mm});
            skLineSegment(sketch, "E3.15.2.0", {"start": v(18.42, 12.07) * mm, "end": v(19.69, 12.07) * mm});
            skLineSegment(sketch, "E3.15.2.1", {"start": v(18.42, 12.07) * mm, "end": v(18.42, 10.8) * mm});
            skLineSegment(sketch, "E3.15.2.2", {"start": v(19.69, 12.07) * mm, "end": v(19.69, 10.8) * mm});
            skLineSegment(sketch, "E3.15.2.3", {"start": v(18.42, 10.8) * mm, "end": v(19.69, 10.8) * mm});
            skLineSegment(sketch, "E3.15.3.0", {"start": v(18.42, 9.53) * mm, "end": v(19.69, 9.53) * mm});
            skLineSegment(sketch, "E3.15.3.1", {"start": v(18.42, 9.53) * mm, "end": v(18.42, 8.26) * mm});
            skLineSegment(sketch, "E3.15.3.2", {"start": v(19.69, 9.53) * mm, "end": v(19.69, 8.26) * mm});
            skLineSegment(sketch, "E3.15.3.3", {"start": v(18.42, 8.26) * mm, "end": v(19.69, 8.26) * mm});
            skLineSegment(sketch, "E3.15.4.0", {"start": v(18.42, 6.99) * mm, "end": v(19.69, 6.99) * mm});
            skLineSegment(sketch, "E3.15.4.1", {"start": v(18.42, 6.99) * mm, "end": v(18.42, 5.72) * mm});
            skLineSegment(sketch, "E3.15.4.2", {"start": v(19.69, 6.99) * mm, "end": v(19.69, 5.72) * mm});
            skLineSegment(sketch, "E3.15.4.3", {"start": v(18.42, 5.72) * mm, "end": v(19.69, 5.72) * mm});
            skLineSegment(sketch, "E3.direction1", {"start": v(-19.69, 17.15) * mm, "end": v(-17.15, 17.15) * mm, "construction": true});
            skLineSegment(sketch, "E3.direction2", {"start": v(-19.69, 17.15) * mm, "end": v(-19.69, 14.6) * mm, "construction": true});
            skLineSegment(sketch, "E4.MirrorCS", {"start": v(18.42, -6.99) * mm, "end": v(18.42, -5.72) * mm});
            skLineSegment(sketch, "E5.MirrorCS", {"start": v(18.42, -17.15) * mm, "end": v(18.42, -15.88) * mm});
            skLineSegment(sketch, "E6.MirrorCS", {"start": v(-17.15, -12.07) * mm, "end": v(-17.15, -10.8) * mm});
            skLineSegment(sketch, "E7.MirrorCS", {"start": v(-9.53, -9.53) * mm, "end": v(-9.53, -8.26) * mm});
            skLineSegment(sketch, "E8.MirrorCS", {"start": v(-12.07, -6.99) * mm, "end": v(-12.07, -5.72) * mm});
            skLineSegment(sketch, "E9.MirrorCS", {"start": v(-12.07, -17.15) * mm, "end": v(-12.07, -15.88) * mm});
            skLineSegment(sketch, "E10.MirrorCS", {"start": v(-14.6, -14.6) * mm, "end": v(-14.6, -13.34) * mm});
            skLineSegment(sketch, "E11.MirrorCS", {"start": v(-1.9, -6.99) * mm, "end": v(-1.9, -5.72) * mm});
            skLineSegment(sketch, "E12.MirrorCS", {"start": v(-1.9, -17.15) * mm, "end": v(-1.9, -15.88) * mm});
            skLineSegment(sketch, "E13.MirrorCS", {"start": v(-4.45, -14.6) * mm, "end": v(-4.45, -13.34) * mm});
            skLineSegment(sketch, "E14.MirrorCS", {"start": v(-6.99, -12.07) * mm, "end": v(-6.99, -10.8) * mm});
            skLineSegment(sketch, "E15.MirrorCS", {"start": v(8.26, -17.15) * mm, "end": v(8.26, -15.88) * mm});
            skLineSegment(sketch, "E16.MirrorCS", {"start": v(5.72, -14.6) * mm, "end": v(5.72, -13.34) * mm});
            skLineSegment(sketch, "E17.MirrorCS", {"start": v(3.18, -12.07) * mm, "end": v(3.18, -10.8) * mm});
            skLineSegment(sketch, "E18.MirrorCS", {"start": v(0.64, -9.53) * mm, "end": v(0.64, -8.26) * mm});
            skLineSegment(sketch, "E19.MirrorCS", {"start": v(15.88, -14.6) * mm, "end": v(15.88, -13.34) * mm});
            skLineSegment(sketch, "E20.MirrorCS", {"start": v(13.34, -12.07) * mm, "end": v(13.34, -10.8) * mm});
            skLineSegment(sketch, "E21.MirrorCS", {"start": v(10.8, -9.53) * mm, "end": v(10.8, -8.26) * mm});
            skLineSegment(sketch, "E22.MirrorCS", {"start": v(8.26, -6.99) * mm, "end": v(8.26, -5.72) * mm});
            skLineSegment(sketch, "E23.MirrorCS", {"start": v(-15.88, -12.07) * mm, "end": v(-15.88, -10.8) * mm});
            skLineSegment(sketch, "E24.MirrorCS", {"start": v(-8.26, -9.53) * mm, "end": v(-8.26, -8.26) * mm});
            skLineSegment(sketch, "E25.MirrorCS", {"start": v(-10.8, -6.99) * mm, "end": v(-10.8, -5.72) * mm});
            skLineSegment(sketch, "E26.MirrorCS", {"start": v(-10.8, -17.15) * mm, "end": v(-10.8, -15.88) * mm});
            skLineSegment(sketch, "E27.MirrorCS", {"start": v(-13.34, -14.6) * mm, "end": v(-13.34, -13.34) * mm});
            skLineSegment(sketch, "E28.MirrorCS", {"start": v(-0.63, -6.99) * mm, "end": v(-0.64, -5.72) * mm});
            skLineSegment(sketch, "E29.MirrorCS", {"start": v(-0.63, -17.15) * mm, "end": v(-0.64, -15.88) * mm});
            skLineSegment(sketch, "E30.MirrorCS", {"start": v(-3.18, -14.6) * mm, "end": v(-3.18, -13.34) * mm});
            skLineSegment(sketch, "E31.MirrorCS", {"start": v(-5.72, -12.07) * mm, "end": v(-5.72, -10.8) * mm});
            skLineSegment(sketch, "E32.MirrorCS", {"start": v(9.53, -17.15) * mm, "end": v(9.53, -15.88) * mm});
            skLineSegment(sketch, "E33.MirrorCS", {"start": v(6.99, -14.6) * mm, "end": v(6.99, -13.34) * mm});
            skLineSegment(sketch, "E34.MirrorCS", {"start": v(4.45, -12.07) * mm, "end": v(4.45, -10.8) * mm});
            skLineSegment(sketch, "E35.MirrorCS", {"start": v(1.9, -9.53) * mm, "end": v(1.9, -8.26) * mm});
            skLineSegment(sketch, "E36.MirrorCS", {"start": v(17.15, -14.6) * mm, "end": v(17.15, -13.34) * mm});
            skLineSegment(sketch, "E37.MirrorCS", {"start": v(14.6, -12.07) * mm, "end": v(14.6, -10.8) * mm});
            skLineSegment(sketch, "E38.MirrorCS", {"start": v(12.07, -9.53) * mm, "end": v(12.07, -8.26) * mm});
            skLineSegment(sketch, "E39.MirrorCS", {"start": v(9.53, -6.99) * mm, "end": v(9.53, -5.72) * mm});
            skLineSegment(sketch, "E40.MirrorCS", {"start": v(19.69, -6.99) * mm, "end": v(19.69, -5.72) * mm});
            skLineSegment(sketch, "E41.MirrorCS", {"start": v(19.69, -17.15) * mm, "end": v(19.69, -15.88) * mm});
            skLineSegment(sketch, "E42.MirrorCS", {"start": v(-17.15, -10.8) * mm, "end": v(-15.88, -10.8) * mm});
            skLineSegment(sketch, "E43.MirrorCS", {"start": v(-9.53, -8.26) * mm, "end": v(-8.26, -8.26) * mm});
            skLineSegment(sketch, "E44.MirrorCS", {"start": v(-12.07, -5.72) * mm, "end": v(-10.8, -5.72) * mm});
            skLineSegment(sketch, "E45.MirrorCS", {"start": v(-12.07, -15.88) * mm, "end": v(-10.8, -15.88) * mm});
            skLineSegment(sketch, "E46.MirrorCS", {"start": v(-14.6, -13.34) * mm, "end": v(-13.34, -13.34) * mm});
            skLineSegment(sketch, "E47.MirrorCS", {"start": v(-1.9, -5.72) * mm, "end": v(-0.64, -5.72) * mm});
            skLineSegment(sketch, "E48.MirrorCS", {"start": v(-1.9, -15.88) * mm, "end": v(-0.64, -15.88) * mm});
            skLineSegment(sketch, "E49.MirrorCS", {"start": v(-4.45, -13.34) * mm, "end": v(-3.18, -13.34) * mm});
            skLineSegment(sketch, "E50.MirrorCS", {"start": v(-6.99, -10.8) * mm, "end": v(-5.72, -10.8) * mm});
            skLineSegment(sketch, "E51.MirrorCS", {"start": v(8.26, -15.88) * mm, "end": v(9.53, -15.88) * mm});
            skLineSegment(sketch, "E52.MirrorCS", {"start": v(5.72, -13.34) * mm, "end": v(6.99, -13.34) * mm});
            skLineSegment(sketch, "E53.MirrorCS", {"start": v(3.18, -10.8) * mm, "end": v(4.45, -10.8) * mm});
            skLineSegment(sketch, "E54.MirrorCS", {"start": v(0.64, -8.26) * mm, "end": v(1.9, -8.26) * mm});
            skLineSegment(sketch, "E55.MirrorCS", {"start": v(15.88, -13.34) * mm, "end": v(17.15, -13.34) * mm});
            skLineSegment(sketch, "E56.MirrorCS", {"start": v(13.34, -10.8) * mm, "end": v(14.6, -10.8) * mm});
            skLineSegment(sketch, "E57.MirrorCS", {"start": v(10.8, -8.26) * mm, "end": v(12.07, -8.26) * mm});
            skLineSegment(sketch, "E58.MirrorCS", {"start": v(8.26, -5.72) * mm, "end": v(9.53, -5.72) * mm});
            skLineSegment(sketch, "E59.MirrorCS", {"start": v(18.42, -5.72) * mm, "end": v(19.69, -5.72) * mm});
            skLineSegment(sketch, "E60.MirrorCS", {"start": v(18.42, -15.88) * mm, "end": v(19.69, -15.88) * mm});
            skLineSegment(sketch, "E61.MirrorCS", {"start": v(-9.53, -6.99) * mm, "end": v(-8.26, -6.99) * mm});
            skLineSegment(sketch, "E62.MirrorCS", {"start": v(-9.53, -17.15) * mm, "end": v(-8.26, -17.15) * mm});
            skLineSegment(sketch, "E63.MirrorCS", {"start": v(-12.07, -14.6) * mm, "end": v(-10.8, -14.6) * mm});
            skLineSegment(sketch, "E64.MirrorCS", {"start": v(-14.6, -12.07) * mm, "end": v(-13.34, -12.07) * mm});
            skLineSegment(sketch, "E65.MirrorCS", {"start": v(0.64, -17.15) * mm, "end": v(1.9, -17.15) * mm});
            skLineSegment(sketch, "E66.MirrorCS", {"start": v(-1.9, -14.6) * mm, "end": v(-0.64, -14.6) * mm});
            skLineSegment(sketch, "E67.MirrorCS", {"start": v(-4.45, -12.07) * mm, "end": v(-3.18, -12.07) * mm});
            skLineSegment(sketch, "E68.MirrorCS", {"start": v(-6.99, -9.53) * mm, "end": v(-5.72, -9.53) * mm});
            skLineSegment(sketch, "E69.MirrorCS", {"start": v(8.26, -14.6) * mm, "end": v(9.53, -14.6) * mm});
            skLineSegment(sketch, "E70.MirrorCS", {"start": v(5.72, -12.07) * mm, "end": v(6.99, -12.07) * mm});
            skLineSegment(sketch, "E71.MirrorCS", {"start": v(3.18, -9.53) * mm, "end": v(4.45, -9.53) * mm});
            skLineSegment(sketch, "E72.MirrorCS", {"start": v(0.64, -6.99) * mm, "end": v(1.9, -6.99) * mm});
            skLineSegment(sketch, "E73.MirrorCS", {"start": v(15.88, -12.07) * mm, "end": v(17.15, -12.07) * mm});
            skLineSegment(sketch, "E74.MirrorCS", {"start": v(13.34, -9.53) * mm, "end": v(14.6, -9.53) * mm});
            skLineSegment(sketch, "E75.MirrorCS", {"start": v(10.8, -6.99) * mm, "end": v(12.07, -6.99) * mm});
            skLineSegment(sketch, "E76.MirrorCS", {"start": v(10.8, -17.15) * mm, "end": v(12.07, -17.15) * mm});
            skLineSegment(sketch, "E77.MirrorCS", {"start": v(18.42, -14.6) * mm, "end": v(19.69, -14.6) * mm});
            skLineSegment(sketch, "E78.MirrorCS", {"start": v(-17.15, -9.53) * mm, "end": v(-15.88, -9.53) * mm});
            skLineSegment(sketch, "E79.MirrorCS", {"start": v(-19.69, -6.99) * mm, "end": v(-18.42, -6.99) * mm});
            skLineSegment(sketch, "E80.MirrorCS", {"start": v(0.64, -17.15) * mm, "end": v(0.64, -15.88) * mm});
            skLineSegment(sketch, "E81.MirrorCS", {"start": v(-1.9, -14.6) * mm, "end": v(-1.9, -13.34) * mm});
            skLineSegment(sketch, "E82.MirrorCS", {"start": v(-4.45, -12.07) * mm, "end": v(-4.45, -10.8) * mm});
            skLineSegment(sketch, "E83.MirrorCS", {"start": v(-6.99, -9.53) * mm, "end": v(-6.99, -8.26) * mm});
            skLineSegment(sketch, "E84.MirrorCS", {"start": v(8.26, -14.6) * mm, "end": v(8.26, -13.34) * mm});
            skLineSegment(sketch, "E85.MirrorCS", {"start": v(5.72, -12.07) * mm, "end": v(5.72, -10.8) * mm});
            skLineSegment(sketch, "E86.MirrorCS", {"start": v(3.18, -9.53) * mm, "end": v(3.18, -8.26) * mm});
            skLineSegment(sketch, "E87.MirrorCS", {"start": v(0.64, -6.99) * mm, "end": v(0.64, -5.72) * mm});
            skLineSegment(sketch, "E88.MirrorCS", {"start": v(15.88, -12.07) * mm, "end": v(15.88, -10.8) * mm});
            skLineSegment(sketch, "E89.MirrorCS", {"start": v(13.34, -9.53) * mm, "end": v(13.34, -8.26) * mm});
            skLineSegment(sketch, "E90.MirrorCS", {"start": v(10.8, -6.99) * mm, "end": v(10.8, -5.72) * mm});
            skLineSegment(sketch, "E91.MirrorCS", {"start": v(10.8, -17.15) * mm, "end": v(10.8, -15.88) * mm});
            skLineSegment(sketch, "E92.MirrorCS", {"start": v(18.42, -14.6) * mm, "end": v(18.42, -13.34) * mm});
            skLineSegment(sketch, "E93.MirrorCS", {"start": v(-17.15, -9.53) * mm, "end": v(-17.15, -8.26) * mm});
            skLineSegment(sketch, "E94.MirrorCS", {"start": v(-19.69, -6.99) * mm, "end": v(-19.69, -5.72) * mm});
            skLineSegment(sketch, "E95.MirrorCS", {"start": v(-9.53, -6.99) * mm, "end": v(-9.53, -5.72) * mm});
            skLineSegment(sketch, "E96.MirrorCS", {"start": v(-9.53, -17.15) * mm, "end": v(-9.53, -15.88) * mm});
            skLineSegment(sketch, "E97.MirrorCS", {"start": v(-12.07, -14.6) * mm, "end": v(-12.07, -13.34) * mm});
            skLineSegment(sketch, "E98.MirrorCS", {"start": v(-14.6, -12.07) * mm, "end": v(-14.6, -10.8) * mm});
            skLineSegment(sketch, "E99.MirrorCS", {"start": v(9.53, -14.6) * mm, "end": v(9.53, -13.34) * mm});
            skLineSegment(sketch, "E100.MirrorCS", {"start": v(6.99, -12.07) * mm, "end": v(6.99, -10.8) * mm});
            skLineSegment(sketch, "E101.MirrorCS", {"start": v(4.45, -9.53) * mm, "end": v(4.45, -8.26) * mm});
            skLineSegment(sketch, "E102.MirrorCS", {"start": v(1.9, -6.99) * mm, "end": v(1.9, -5.72) * mm});
            skLineSegment(sketch, "E103.MirrorCS", {"start": v(17.15, -12.07) * mm, "end": v(17.15, -10.8) * mm});
            skLineSegment(sketch, "E104.MirrorCS", {"start": v(14.6, -9.53) * mm, "end": v(14.6, -8.26) * mm});
            skLineSegment(sketch, "E105.MirrorCS", {"start": v(12.07, -6.99) * mm, "end": v(12.07, -5.72) * mm});
            skLineSegment(sketch, "E106.MirrorCS", {"start": v(12.07, -17.15) * mm, "end": v(12.07, -15.88) * mm});
            skLineSegment(sketch, "E107.MirrorCS", {"start": v(19.69, -14.6) * mm, "end": v(19.69, -13.34) * mm});
            skLineSegment(sketch, "E108.MirrorCS", {"start": v(-15.88, -9.53) * mm, "end": v(-15.88, -8.26) * mm});
            skLineSegment(sketch, "E109.MirrorCS", {"start": v(-18.42, -6.99) * mm, "end": v(-18.42, -5.72) * mm});
            skLineSegment(sketch, "E110.MirrorCS", {"start": v(-8.26, -6.99) * mm, "end": v(-8.26, -5.72) * mm});
            skLineSegment(sketch, "E111.MirrorCS", {"start": v(-8.26, -17.15) * mm, "end": v(-8.26, -15.88) * mm});
            skLineSegment(sketch, "E112.MirrorCS", {"start": v(-10.8, -14.6) * mm, "end": v(-10.8, -13.34) * mm});
            skLineSegment(sketch, "E113.MirrorCS", {"start": v(-13.34, -12.07) * mm, "end": v(-13.34, -10.8) * mm});
            skLineSegment(sketch, "E114.MirrorCS", {"start": v(1.9, -17.15) * mm, "end": v(1.9, -15.88) * mm});
            skLineSegment(sketch, "E115.MirrorCS", {"start": v(-0.63, -14.6) * mm, "end": v(-0.64, -13.34) * mm});
            skLineSegment(sketch, "E116.MirrorCS", {"start": v(-3.18, -12.07) * mm, "end": v(-3.18, -10.8) * mm});
            skLineSegment(sketch, "E117.MirrorCS", {"start": v(-5.72, -9.53) * mm, "end": v(-5.72, -8.26) * mm});
            skLineSegment(sketch, "E118.MirrorCS", {"start": v(15.88, -10.8) * mm, "end": v(17.15, -10.8) * mm});
            skLineSegment(sketch, "E119.MirrorCS", {"start": v(13.34, -8.26) * mm, "end": v(14.6, -8.26) * mm});
            skLineSegment(sketch, "E120.MirrorCS", {"start": v(10.8, -5.72) * mm, "end": v(12.07, -5.72) * mm});
            skLineSegment(sketch, "E121.MirrorCS", {"start": v(10.8, -15.88) * mm, "end": v(12.07, -15.88) * mm});
            skLineSegment(sketch, "E122.MirrorCS", {"start": v(18.42, -13.34) * mm, "end": v(19.69, -13.34) * mm});
            skLineSegment(sketch, "E123.MirrorCS", {"start": v(-17.15, -8.26) * mm, "end": v(-15.88, -8.26) * mm});
            skLineSegment(sketch, "E124.MirrorCS", {"start": v(-19.69, -5.72) * mm, "end": v(-18.42, -5.72) * mm});
            skLineSegment(sketch, "E125.MirrorCS", {"start": v(-9.53, -5.72) * mm, "end": v(-8.26, -5.72) * mm});
            skLineSegment(sketch, "E126.MirrorCS", {"start": v(-9.53, -15.88) * mm, "end": v(-8.26, -15.88) * mm});
            skLineSegment(sketch, "E127.MirrorCS", {"start": v(-12.07, -13.34) * mm, "end": v(-10.8, -13.34) * mm});
            skLineSegment(sketch, "E128.MirrorCS", {"start": v(-14.6, -10.8) * mm, "end": v(-13.34, -10.8) * mm});
            skLineSegment(sketch, "E129.MirrorCS", {"start": v(0.64, -15.88) * mm, "end": v(1.9, -15.88) * mm});
            skLineSegment(sketch, "E130.MirrorCS", {"start": v(-1.9, -13.34) * mm, "end": v(-0.64, -13.34) * mm});
            skLineSegment(sketch, "E131.MirrorCS", {"start": v(-4.45, -10.8) * mm, "end": v(-3.18, -10.8) * mm});
            skLineSegment(sketch, "E132.MirrorCS", {"start": v(-6.99, -8.26) * mm, "end": v(-5.72, -8.26) * mm});
            skLineSegment(sketch, "E133.MirrorCS", {"start": v(8.26, -13.34) * mm, "end": v(9.53, -13.34) * mm});
            skLineSegment(sketch, "E134.MirrorCS", {"start": v(5.72, -10.8) * mm, "end": v(6.99, -10.8) * mm});
            skLineSegment(sketch, "E135.MirrorCS", {"start": v(3.18, -8.26) * mm, "end": v(4.45, -8.26) * mm});
            skLineSegment(sketch, "E136.MirrorCS", {"start": v(0.64, -5.72) * mm, "end": v(1.9, -5.72) * mm});
            skLineSegment(sketch, "E137.MirrorCS", {"start": v(18.42, -12.07) * mm, "end": v(19.69, -12.07) * mm});
            skLineSegment(sketch, "E138.MirrorCS", {"start": v(-17.15, -6.99) * mm, "end": v(-15.88, -6.99) * mm});
            skLineSegment(sketch, "E139.MirrorCS", {"start": v(-17.15, -17.15) * mm, "end": v(-15.88, -17.15) * mm});
            skLineSegment(sketch, "E140.MirrorCS", {"start": v(-6.99, -17.15) * mm, "end": v(-5.72, -17.15) * mm});
            skLineSegment(sketch, "E141.MirrorCS", {"start": v(-9.53, -14.6) * mm, "end": v(-8.26, -14.6) * mm});
            skLineSegment(sketch, "E142.MirrorCS", {"start": v(-12.07, -12.07) * mm, "end": v(-10.8, -12.07) * mm});
            skLineSegment(sketch, "E143.MirrorCS", {"start": v(-14.6, -9.53) * mm, "end": v(-13.34, -9.53) * mm});
            skLineSegment(sketch, "E144.MirrorCS", {"start": v(0.64, -14.6) * mm, "end": v(1.9, -14.6) * mm});
            skLineSegment(sketch, "E145.MirrorCS", {"start": v(-1.9, -12.07) * mm, "end": v(-0.64, -12.07) * mm});
            skLineSegment(sketch, "E146.MirrorCS", {"start": v(-4.45, -9.53) * mm, "end": v(-3.18, -9.53) * mm});
            skLineSegment(sketch, "E147.MirrorCS", {"start": v(-6.99, -6.99) * mm, "end": v(-5.72, -6.99) * mm});
            skLineSegment(sketch, "E148.MirrorCS", {"start": v(8.26, -12.07) * mm, "end": v(9.53, -12.07) * mm});
            skLineSegment(sketch, "E149.MirrorCS", {"start": v(5.72, -9.53) * mm, "end": v(6.99, -9.53) * mm});
            skLineSegment(sketch, "E150.MirrorCS", {"start": v(3.18, -6.99) * mm, "end": v(4.45, -6.99) * mm});
            skLineSegment(sketch, "E151.MirrorCS", {"start": v(3.18, -17.15) * mm, "end": v(4.45, -17.15) * mm});
            skLineSegment(sketch, "E152.MirrorCS", {"start": v(15.88, -9.53) * mm, "end": v(17.15, -9.53) * mm});
            skLineSegment(sketch, "E153.MirrorCS", {"start": v(13.34, -6.99) * mm, "end": v(14.6, -6.99) * mm});
            skLineSegment(sketch, "E154.MirrorCS", {"start": v(13.34, -17.15) * mm, "end": v(14.6, -17.15) * mm});
            skLineSegment(sketch, "E155.MirrorCS", {"start": v(10.8, -14.6) * mm, "end": v(12.07, -14.6) * mm});
            skLineSegment(sketch, "E156.MirrorCS", {"start": v(-17.15, -6.99) * mm, "end": v(-17.15, -5.72) * mm});
            skLineSegment(sketch, "E157.MirrorCS", {"start": v(-17.15, -17.15) * mm, "end": v(-17.15, -15.88) * mm});
            skLineSegment(sketch, "E158.MirrorCS", {"start": v(-6.99, -17.15) * mm, "end": v(-6.99, -15.88) * mm});
            skLineSegment(sketch, "E159.MirrorCS", {"start": v(-9.53, -14.6) * mm, "end": v(-9.53, -13.34) * mm});
            skLineSegment(sketch, "E160.MirrorCS", {"start": v(-12.07, -12.07) * mm, "end": v(-12.07, -10.8) * mm});
            skLineSegment(sketch, "E161.MirrorCS", {"start": v(-14.6, -9.53) * mm, "end": v(-14.6, -8.26) * mm});
            skLineSegment(sketch, "E162.MirrorCS", {"start": v(0.64, -14.6) * mm, "end": v(0.64, -13.34) * mm});
            skLineSegment(sketch, "E163.MirrorCS", {"start": v(-1.9, -12.07) * mm, "end": v(-1.9, -10.8) * mm});
            skLineSegment(sketch, "E164.MirrorCS", {"start": v(-4.45, -9.53) * mm, "end": v(-4.45, -8.26) * mm});
            skLineSegment(sketch, "E165.MirrorCS", {"start": v(-6.99, -6.99) * mm, "end": v(-6.99, -5.72) * mm});
            skLineSegment(sketch, "E166.MirrorCS", {"start": v(8.26, -12.07) * mm, "end": v(8.26, -10.8) * mm});
            skLineSegment(sketch, "E167.MirrorCS", {"start": v(5.72, -9.53) * mm, "end": v(5.72, -8.26) * mm});
            skLineSegment(sketch, "E168.MirrorCS", {"start": v(3.18, -6.99) * mm, "end": v(3.18, -5.72) * mm});
            skLineSegment(sketch, "E169.MirrorCS", {"start": v(3.18, -17.15) * mm, "end": v(3.18, -15.88) * mm});
            skLineSegment(sketch, "E170.MirrorCS", {"start": v(15.88, -9.53) * mm, "end": v(15.88, -8.26) * mm});
            skLineSegment(sketch, "E171.MirrorCS", {"start": v(13.34, -6.99) * mm, "end": v(13.34, -5.72) * mm});
            skLineSegment(sketch, "E172.MirrorCS", {"start": v(13.34, -17.15) * mm, "end": v(13.34, -15.88) * mm});
            skLineSegment(sketch, "E173.MirrorCS", {"start": v(10.8, -14.6) * mm, "end": v(10.8, -13.34) * mm});
            skLineSegment(sketch, "E174.MirrorCS", {"start": v(18.42, -12.07) * mm, "end": v(18.42, -10.8) * mm});
            skLineSegment(sketch, "E175.MirrorCS", {"start": v(-15.88, -6.99) * mm, "end": v(-15.88, -5.72) * mm});
            skLineSegment(sketch, "E176.MirrorCS", {"start": v(-15.88, -17.15) * mm, "end": v(-15.88, -15.88) * mm});
            skLineSegment(sketch, "E177.MirrorCS", {"start": v(-8.26, -14.6) * mm, "end": v(-8.26, -13.34) * mm});
            skLineSegment(sketch, "E178.MirrorCS", {"start": v(-5.72, -17.15) * mm, "end": v(-5.72, -15.88) * mm});
            skLineSegment(sketch, "E179.MirrorCS", {"start": v(-10.8, -12.07) * mm, "end": v(-10.8, -10.8) * mm});
            skLineSegment(sketch, "E180.MirrorCS", {"start": v(-13.34, -9.53) * mm, "end": v(-13.34, -8.26) * mm});
            skLineSegment(sketch, "E181.MirrorCS", {"start": v(1.9, -14.6) * mm, "end": v(1.9, -13.34) * mm});
            skLineSegment(sketch, "E182.MirrorCS", {"start": v(-0.63, -12.07) * mm, "end": v(-0.64, -10.8) * mm});
            skLineSegment(sketch, "E183.MirrorCS", {"start": v(-3.18, -9.53) * mm, "end": v(-3.18, -8.26) * mm});
            skLineSegment(sketch, "E184.MirrorCS", {"start": v(-5.72, -6.99) * mm, "end": v(-5.72, -5.72) * mm});
            skLineSegment(sketch, "E185.MirrorCS", {"start": v(9.53, -12.07) * mm, "end": v(9.53, -10.8) * mm});
            skLineSegment(sketch, "E186.MirrorCS", {"start": v(6.99, -9.53) * mm, "end": v(6.99, -8.26) * mm});
            skLineSegment(sketch, "E187.MirrorCS", {"start": v(4.45, -6.99) * mm, "end": v(4.45, -5.72) * mm});
            skLineSegment(sketch, "E188.MirrorCS", {"start": v(17.15, -9.53) * mm, "end": v(17.15, -8.26) * mm});
            skLineSegment(sketch, "E189.MirrorCS", {"start": v(4.45, -17.15) * mm, "end": v(4.45, -15.88) * mm});
            skLineSegment(sketch, "E190.MirrorCS", {"start": v(14.6, -6.99) * mm, "end": v(14.6, -5.72) * mm});
            skLineSegment(sketch, "E191.MirrorCS", {"start": v(14.6, -17.15) * mm, "end": v(14.6, -15.88) * mm});
            skLineSegment(sketch, "E192.MirrorCS", {"start": v(19.69, -12.07) * mm, "end": v(19.69, -10.8) * mm});
            skLineSegment(sketch, "E193.MirrorCS", {"start": v(12.07, -14.6) * mm, "end": v(12.07, -13.34) * mm});
            skLineSegment(sketch, "E194.MirrorCS", {"start": v(-12.07, -10.8) * mm, "end": v(-10.8, -10.8) * mm});
            skLineSegment(sketch, "E195.MirrorCS", {"start": v(-14.6, -8.26) * mm, "end": v(-13.34, -8.26) * mm});
            skLineSegment(sketch, "E196.MirrorCS", {"start": v(-17.15, -5.72) * mm, "end": v(-15.88, -5.72) * mm});
            skLineSegment(sketch, "E197.MirrorCS", {"start": v(-17.15, -15.88) * mm, "end": v(-15.88, -15.88) * mm});
            skLineSegment(sketch, "E198.MirrorCS", {"start": v(-4.45, -8.26) * mm, "end": v(-3.18, -8.26) * mm});
            skLineSegment(sketch, "E199.MirrorCS", {"start": v(-6.99, -5.72) * mm, "end": v(-5.72, -5.72) * mm});
            skLineSegment(sketch, "E200.MirrorCS", {"start": v(-6.99, -15.88) * mm, "end": v(-5.72, -15.88) * mm});
            skLineSegment(sketch, "E201.MirrorCS", {"start": v(-9.53, -13.34) * mm, "end": v(-8.26, -13.34) * mm});
            skLineSegment(sketch, "E202.MirrorCS", {"start": v(3.18, -5.72) * mm, "end": v(4.45, -5.72) * mm});
            skLineSegment(sketch, "E203.MirrorCS", {"start": v(3.18, -15.88) * mm, "end": v(4.45, -15.88) * mm});
            skLineSegment(sketch, "E204.MirrorCS", {"start": v(0.64, -13.34) * mm, "end": v(1.9, -13.34) * mm});
            skLineSegment(sketch, "E205.MirrorCS", {"start": v(-1.9, -10.8) * mm, "end": v(-0.64, -10.8) * mm});
            skLineSegment(sketch, "E206.MirrorCS", {"start": v(13.34, -15.88) * mm, "end": v(14.6, -15.88) * mm});
            skLineSegment(sketch, "E207.MirrorCS", {"start": v(10.8, -13.34) * mm, "end": v(12.07, -13.34) * mm});
            skLineSegment(sketch, "E208.MirrorCS", {"start": v(8.26, -10.8) * mm, "end": v(9.53, -10.8) * mm});
            skLineSegment(sketch, "E209.MirrorCS", {"start": v(5.72, -8.26) * mm, "end": v(6.99, -8.26) * mm});
            skLineSegment(sketch, "E210.MirrorCS", {"start": v(18.42, -10.8) * mm, "end": v(19.69, -10.8) * mm});
            skLineSegment(sketch, "E211.MirrorCS", {"start": v(15.88, -8.26) * mm, "end": v(17.15, -8.26) * mm});
            skLineSegment(sketch, "E212.MirrorCS", {"start": v(13.34, -5.72) * mm, "end": v(14.6, -5.72) * mm});
            skLineSegment(sketch, "E213.MirrorCS", {"start": v(-12.07, -9.53) * mm, "end": v(-10.8, -9.53) * mm});
            skLineSegment(sketch, "E214.MirrorCS", {"start": v(-14.6, -6.99) * mm, "end": v(-13.34, -6.99) * mm});
            skLineSegment(sketch, "E215.MirrorCS", {"start": v(-14.6, -17.15) * mm, "end": v(-13.34, -17.15) * mm});
            skLineSegment(sketch, "E216.MirrorCS", {"start": v(-17.15, -14.6) * mm, "end": v(-15.88, -14.6) * mm});
            skLineSegment(sketch, "E217.MirrorCS", {"start": v(-4.45, -6.99) * mm, "end": v(-3.18, -6.99) * mm});
            skLineSegment(sketch, "E218.MirrorCS", {"start": v(-4.45, -17.15) * mm, "end": v(-3.18, -17.15) * mm});
            skLineSegment(sketch, "E219.MirrorCS", {"start": v(-6.99, -14.6) * mm, "end": v(-5.72, -14.6) * mm});
            skLineSegment(sketch, "E220.MirrorCS", {"start": v(-9.53, -12.07) * mm, "end": v(-8.26, -12.07) * mm});
            skLineSegment(sketch, "E221.MirrorCS", {"start": v(5.72, -17.15) * mm, "end": v(6.99, -17.15) * mm});
            skLineSegment(sketch, "E222.MirrorCS", {"start": v(3.18, -14.6) * mm, "end": v(4.45, -14.6) * mm});
            skLineSegment(sketch, "E223.MirrorCS", {"start": v(0.64, -12.07) * mm, "end": v(1.9, -12.07) * mm});
            skLineSegment(sketch, "E224.MirrorCS", {"start": v(-1.9, -9.53) * mm, "end": v(-0.64, -9.53) * mm});
            skLineSegment(sketch, "E225.MirrorCS", {"start": v(13.34, -14.6) * mm, "end": v(14.6, -14.6) * mm});
            skLineSegment(sketch, "E226.MirrorCS", {"start": v(10.8, -12.07) * mm, "end": v(12.07, -12.07) * mm});
            skLineSegment(sketch, "E227.MirrorCS", {"start": v(8.26, -9.53) * mm, "end": v(9.53, -9.53) * mm});
            skLineSegment(sketch, "E228.MirrorCS", {"start": v(5.72, -6.99) * mm, "end": v(6.99, -6.99) * mm});
            skLineSegment(sketch, "E229.MirrorCS", {"start": v(18.42, -9.53) * mm, "end": v(19.69, -9.53) * mm});
            skLineSegment(sketch, "E230.MirrorCS", {"start": v(15.88, -6.99) * mm, "end": v(17.15, -6.99) * mm});
            skLineSegment(sketch, "E231.MirrorCS", {"start": v(15.88, -17.15) * mm, "end": v(17.15, -17.15) * mm});
            skLineSegment(sketch, "E232.MirrorCS", {"start": v(-12.07, -9.53) * mm, "end": v(-12.07, -8.26) * mm});
            skLineSegment(sketch, "E233.MirrorCS", {"start": v(-14.6, -6.99) * mm, "end": v(-14.6, -5.72) * mm});
            skLineSegment(sketch, "E234.MirrorCS", {"start": v(-14.6, -17.15) * mm, "end": v(-14.6, -15.88) * mm});
            skLineSegment(sketch, "E235.MirrorCS", {"start": v(-17.15, -14.6) * mm, "end": v(-17.15, -13.34) * mm});
            skLineSegment(sketch, "E236.MirrorCS", {"start": v(-4.45, -6.99) * mm, "end": v(-4.45, -5.72) * mm});
            skLineSegment(sketch, "E237.MirrorCS", {"start": v(-4.45, -17.15) * mm, "end": v(-4.45, -15.88) * mm});
            skLineSegment(sketch, "E238.MirrorCS", {"start": v(-6.99, -14.6) * mm, "end": v(-6.99, -13.34) * mm});
            skLineSegment(sketch, "E239.MirrorCS", {"start": v(-9.53, -12.07) * mm, "end": v(-9.53, -10.8) * mm});
            skLineSegment(sketch, "E240.MirrorCS", {"start": v(5.72, -17.15) * mm, "end": v(5.72, -15.88) * mm});
            skLineSegment(sketch, "E241.MirrorCS", {"start": v(3.18, -14.6) * mm, "end": v(3.18, -13.34) * mm});
            skLineSegment(sketch, "E242.MirrorCS", {"start": v(0.64, -12.07) * mm, "end": v(0.64, -10.8) * mm});
            skLineSegment(sketch, "E243.MirrorCS", {"start": v(-1.9, -9.53) * mm, "end": v(-1.9, -8.26) * mm});
            skLineSegment(sketch, "E244.MirrorCS", {"start": v(13.34, -14.6) * mm, "end": v(13.34, -13.34) * mm});
            skLineSegment(sketch, "E245.MirrorCS", {"start": v(10.8, -12.07) * mm, "end": v(10.8, -10.8) * mm});
            skLineSegment(sketch, "E246.MirrorCS", {"start": v(8.26, -9.53) * mm, "end": v(8.26, -8.26) * mm});
            skLineSegment(sketch, "E247.MirrorCS", {"start": v(5.72, -6.99) * mm, "end": v(5.72, -5.72) * mm});
            skLineSegment(sketch, "E248.MirrorCS", {"start": v(18.42, -9.53) * mm, "end": v(18.42, -8.26) * mm});
            skLineSegment(sketch, "E249.MirrorCS", {"start": v(15.88, -6.99) * mm, "end": v(15.88, -5.72) * mm});
            skLineSegment(sketch, "E250.MirrorCS", {"start": v(15.88, -17.15) * mm, "end": v(15.88, -15.88) * mm});
            skLineSegment(sketch, "E251.MirrorCS", {"start": v(-10.8, -9.53) * mm, "end": v(-10.8, -8.26) * mm});
            skLineSegment(sketch, "E252.MirrorCS", {"start": v(-13.34, -6.99) * mm, "end": v(-13.34, -5.72) * mm});
            skLineSegment(sketch, "E253.MirrorCS", {"start": v(-13.34, -17.15) * mm, "end": v(-13.34, -15.88) * mm});
            skLineSegment(sketch, "E254.MirrorCS", {"start": v(-15.88, -14.6) * mm, "end": v(-15.88, -13.34) * mm});
            skLineSegment(sketch, "E255.MirrorCS", {"start": v(-3.18, -6.99) * mm, "end": v(-3.18, -5.72) * mm});
            skLineSegment(sketch, "E256.MirrorCS", {"start": v(-3.18, -17.15) * mm, "end": v(-3.18, -15.88) * mm});
            skLineSegment(sketch, "E257.MirrorCS", {"start": v(-5.72, -14.6) * mm, "end": v(-5.72, -13.34) * mm});
            skLineSegment(sketch, "E258.MirrorCS", {"start": v(-8.26, -12.07) * mm, "end": v(-8.26, -10.8) * mm});
            skLineSegment(sketch, "E259.MirrorCS", {"start": v(6.99, -17.15) * mm, "end": v(6.99, -15.88) * mm});
            skLineSegment(sketch, "E260.MirrorCS", {"start": v(4.45, -14.6) * mm, "end": v(4.45, -13.34) * mm});
            skLineSegment(sketch, "E261.MirrorCS", {"start": v(1.9, -12.07) * mm, "end": v(1.9, -10.8) * mm});
            skLineSegment(sketch, "E262.MirrorCS", {"start": v(-0.63, -9.53) * mm, "end": v(-0.64, -8.26) * mm});
            skLineSegment(sketch, "E263.MirrorCS", {"start": v(14.6, -14.6) * mm, "end": v(14.6, -13.34) * mm});
            skLineSegment(sketch, "E264.MirrorCS", {"start": v(12.07, -12.07) * mm, "end": v(12.07, -10.8) * mm});
            skLineSegment(sketch, "E265.MirrorCS", {"start": v(9.53, -9.53) * mm, "end": v(9.53, -8.26) * mm});
            skLineSegment(sketch, "E266.MirrorCS", {"start": v(6.99, -6.99) * mm, "end": v(6.99, -5.72) * mm});
            skLineSegment(sketch, "E267.MirrorCS", {"start": v(19.69, -9.53) * mm, "end": v(19.69, -8.26) * mm});
            skLineSegment(sketch, "E268.MirrorCS", {"start": v(17.15, -6.99) * mm, "end": v(17.15, -5.72) * mm});
            skLineSegment(sketch, "E269.MirrorCS", {"start": v(17.15, -17.15) * mm, "end": v(17.15, -15.88) * mm});
            skLineSegment(sketch, "E270.MirrorCS", {"start": v(-12.07, -8.26) * mm, "end": v(-10.8, -8.26) * mm});
            skLineSegment(sketch, "E271.MirrorCS", {"start": v(-14.6, -5.72) * mm, "end": v(-13.34, -5.72) * mm});
            skLineSegment(sketch, "E272.MirrorCS", {"start": v(-14.6, -15.88) * mm, "end": v(-13.34, -15.88) * mm});
            skLineSegment(sketch, "E273.MirrorCS", {"start": v(-17.15, -13.34) * mm, "end": v(-15.88, -13.34) * mm});
            skLineSegment(sketch, "E274.MirrorCS", {"start": v(-4.45, -5.72) * mm, "end": v(-3.18, -5.72) * mm});
            skLineSegment(sketch, "E275.MirrorCS", {"start": v(-4.45, -15.88) * mm, "end": v(-3.18, -15.88) * mm});
            skLineSegment(sketch, "E276.MirrorCS", {"start": v(-6.99, -13.34) * mm, "end": v(-5.72, -13.34) * mm});
            skLineSegment(sketch, "E277.MirrorCS", {"start": v(-9.53, -10.8) * mm, "end": v(-8.26, -10.8) * mm});
            skLineSegment(sketch, "E278.MirrorCS", {"start": v(5.72, -15.88) * mm, "end": v(6.99, -15.88) * mm});
            skLineSegment(sketch, "E279.MirrorCS", {"start": v(3.18, -13.34) * mm, "end": v(4.45, -13.34) * mm});
            skLineSegment(sketch, "E280.MirrorCS", {"start": v(0.64, -10.8) * mm, "end": v(1.9, -10.8) * mm});
            skLineSegment(sketch, "E281.MirrorCS", {"start": v(-1.9, -8.26) * mm, "end": v(-0.64, -8.26) * mm});
            skLineSegment(sketch, "E282.MirrorCS", {"start": v(13.34, -13.34) * mm, "end": v(14.6, -13.34) * mm});
            skLineSegment(sketch, "E283.MirrorCS", {"start": v(10.8, -10.8) * mm, "end": v(12.07, -10.8) * mm});
            skLineSegment(sketch, "E284.MirrorCS", {"start": v(8.26, -8.26) * mm, "end": v(9.53, -8.26) * mm});
            skLineSegment(sketch, "E285.MirrorCS", {"start": v(5.72, -5.72) * mm, "end": v(6.99, -5.72) * mm});
            skLineSegment(sketch, "E286.MirrorCS", {"start": v(18.42, -8.26) * mm, "end": v(19.69, -8.26) * mm});
            skLineSegment(sketch, "E287.MirrorCS", {"start": v(15.88, -5.72) * mm, "end": v(17.15, -5.72) * mm});
            skLineSegment(sketch, "E288.MirrorCS", {"start": v(15.88, -15.88) * mm, "end": v(17.15, -15.88) * mm});
            skLineSegment(sketch, "E289.MirrorCS", {"start": v(-12.07, -6.99) * mm, "end": v(-10.8, -6.99) * mm});
            skLineSegment(sketch, "E290.MirrorCS", {"start": v(-14.6, -14.6) * mm, "end": v(-13.34, -14.6) * mm});
            skLineSegment(sketch, "E291.MirrorCS", {"start": v(-12.07, -17.15) * mm, "end": v(-10.8, -17.15) * mm});
            skLineSegment(sketch, "E292.MirrorCS", {"start": v(-17.15, -12.07) * mm, "end": v(-15.88, -12.07) * mm});
            skLineSegment(sketch, "E293.MirrorCS", {"start": v(-4.45, -14.6) * mm, "end": v(-3.18, -14.6) * mm});
            skLineSegment(sketch, "E294.MirrorCS", {"start": v(-1.9, -17.15) * mm, "end": v(-0.64, -17.15) * mm});
            skLineSegment(sketch, "E295.MirrorCS", {"start": v(-6.99, -12.07) * mm, "end": v(-5.72, -12.07) * mm});
            skLineSegment(sketch, "E296.MirrorCS", {"start": v(-9.53, -9.53) * mm, "end": v(-8.26, -9.53) * mm});
            skLineSegment(sketch, "E297.MirrorCS", {"start": v(5.72, -14.6) * mm, "end": v(6.99, -14.6) * mm});
            skLineSegment(sketch, "E298.MirrorCS", {"start": v(3.18, -12.07) * mm, "end": v(4.45, -12.07) * mm});
            skLineSegment(sketch, "E299.MirrorCS", {"start": v(0.64, -9.53) * mm, "end": v(1.9, -9.53) * mm});
            skLineSegment(sketch, "E300.MirrorCS", {"start": v(-1.9, -6.99) * mm, "end": v(-0.64, -6.99) * mm});
            skLineSegment(sketch, "E301.MirrorCS", {"start": v(13.34, -12.07) * mm, "end": v(14.6, -12.07) * mm});
            skLineSegment(sketch, "E302.MirrorCS", {"start": v(10.8, -9.53) * mm, "end": v(12.07, -9.53) * mm});
            skLineSegment(sketch, "E303.MirrorCS", {"start": v(8.26, -6.99) * mm, "end": v(9.53, -6.99) * mm});
            skLineSegment(sketch, "E304.MirrorCS", {"start": v(8.26, -17.15) * mm, "end": v(9.53, -17.15) * mm});
            skLineSegment(sketch, "E305.MirrorCS", {"start": v(18.42, -6.99) * mm, "end": v(19.69, -6.99) * mm});
            skLineSegment(sketch, "E306.MirrorCS", {"start": v(18.42, -17.15) * mm, "end": v(19.69, -17.15) * mm});
            skLineSegment(sketch, "E307.MirrorCS", {"start": v(15.88, -14.6) * mm, "end": v(17.15, -14.6) * mm});
            skLineSegment(sketch, "E308.MirrorCS", {"start": v(-19.69, -9.53) * mm, "end": v(-19.69, -8.26) * mm});
            skLineSegment(sketch, "E309.MirrorCS", {"start": v(-18.42, -9.53) * mm, "end": v(-18.42, -8.26) * mm});
            skLineSegment(sketch, "E310.MirrorCS", {"start": v(-19.69, -8.26) * mm, "end": v(-18.42, -8.26) * mm});
            skLineSegment(sketch, "E311.MirrorCS", {"start": v(-19.69, -17.15) * mm, "end": v(-18.42, -17.15) * mm});
            skLineSegment(sketch, "E312.MirrorCS", {"start": v(-19.69, -15.88) * mm, "end": v(-18.42, -15.88) * mm});
            skLineSegment(sketch, "E313.MirrorCS", {"start": v(-19.69, -17.15) * mm, "end": v(-19.69, -15.88) * mm});
            skLineSegment(sketch, "E314.MirrorCS", {"start": v(-18.42, -17.15) * mm, "end": v(-18.42, -15.88) * mm});
            skLineSegment(sketch, "E315.MirrorCS", {"start": v(-19.69, -14.6) * mm, "end": v(-18.42, -14.6) * mm});
            skLineSegment(sketch, "E316.MirrorCS", {"start": v(-19.69, -14.6) * mm, "end": v(-19.69, -13.34) * mm});
            skLineSegment(sketch, "E317.MirrorCS", {"start": v(-18.42, -14.6) * mm, "end": v(-18.42, -13.34) * mm});
            skLineSegment(sketch, "E318.MirrorCS", {"start": v(-19.69, -13.34) * mm, "end": v(-18.42, -13.34) * mm});
            skLineSegment(sketch, "E319.MirrorCS", {"start": v(-19.69, -12.07) * mm, "end": v(-18.42, -12.07) * mm});
            skLineSegment(sketch, "E320.MirrorCS", {"start": v(-19.69, -12.07) * mm, "end": v(-19.69, -10.8) * mm});
            skLineSegment(sketch, "E321.MirrorCS", {"start": v(-18.42, -12.07) * mm, "end": v(-18.42, -10.8) * mm});
            skLineSegment(sketch, "E322.MirrorCS", {"start": v(-19.69, -9.53) * mm, "end": v(-18.42, -9.53) * mm});
            skLineSegment(sketch, "E323.MirrorCS", {"start": v(-19.69, -10.8) * mm, "end": v(-18.42, -10.8) * mm});
            skSolve(sketch);
        }
        {
            var Q0;
            Q0=qSketchRegion(id+"F2",true);
            extrude(context, id + "F3", {"entities" : qUnion([Q0]), "operationType" : NewBodyOperationType.REMOVE, "oppositeDirection" : true, "depth" : 6.35 * mm});
        }
    });
